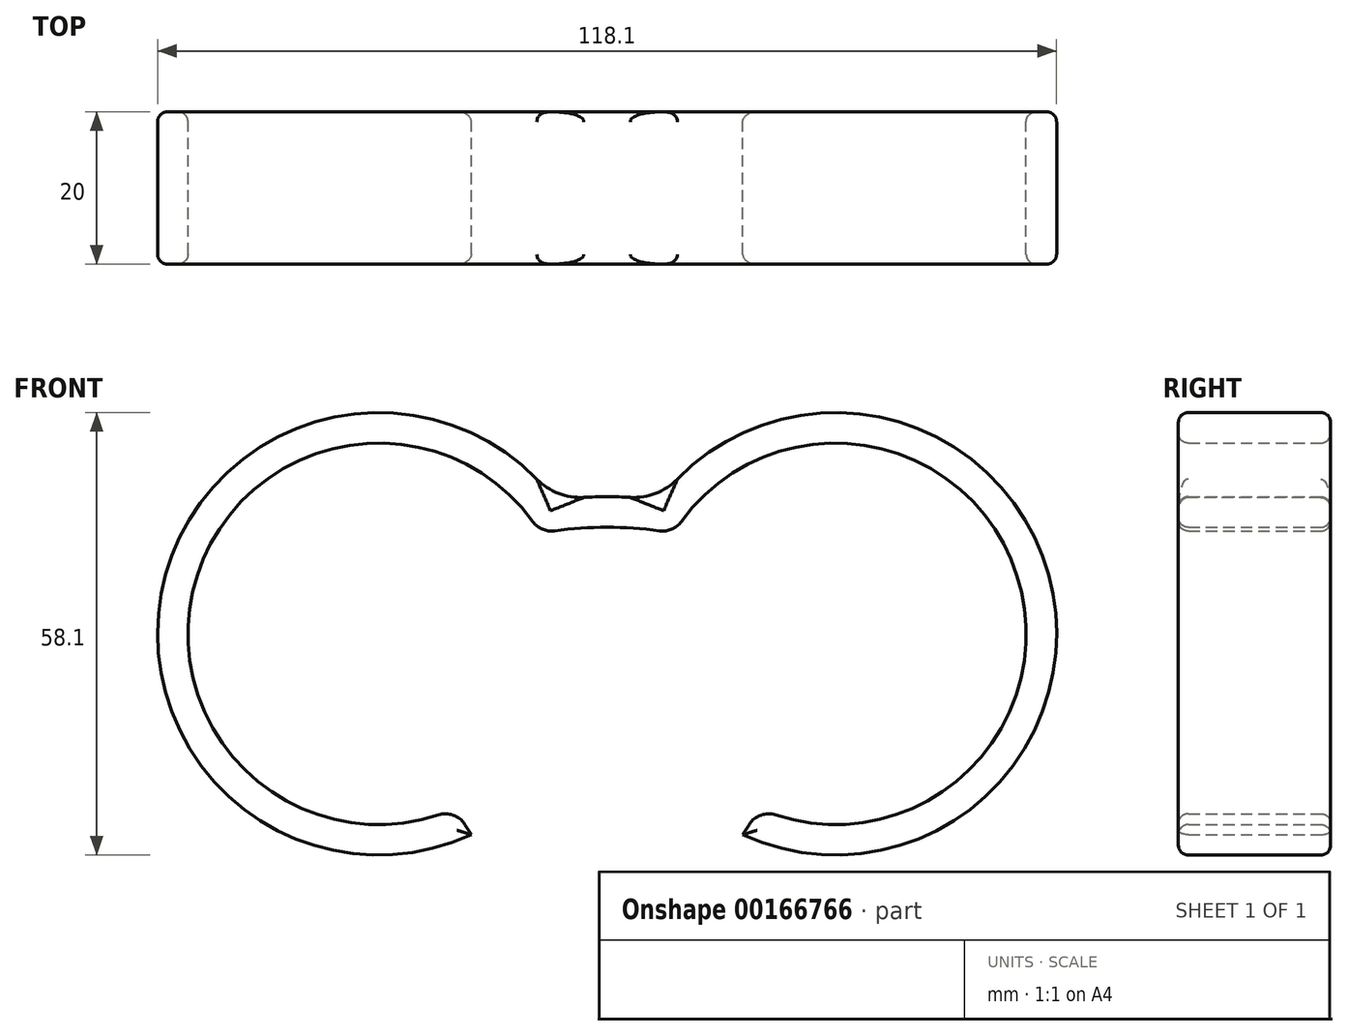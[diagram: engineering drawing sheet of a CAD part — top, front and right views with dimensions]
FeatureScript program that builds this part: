
annotation { "Feature Type Name" : "Feature", "Feature Type Description" : "" }
export const myFeature = defineFeature(function(context is Context, id is Id, definition is map)
    precondition{}
    {
        {
            var Q0;
            Q0=qCreatedBy(makeId("Front.planeOp"),FACE);
            var sketch = newSketch(context, id + "F0", { "sketchPlane" : qUnion([Q0])});
            skArc(sketch, "E0", {"start": v(0, 0) * mm, "mid": v(3.46, -0.12) * mm, "end": v(6.9, -0.48) * mm});
            skLineSegment(sketch, "E1", {"start": v(-31.28, -14) * mm, "end": v(36.53, -14) * mm, "construction": true});
            skPoint(sketch, "E2", {"position": v(30, -14) * mm});
            skLineSegment(sketch, "E3", {"start": v(20, -52.37) * mm, "end": v(20, 23.3) * mm, "construction": true});
            skArc(sketch, "E4", {"start": v(9.74, 0.73) * mm, "mid": v(53.84, -6.31) * mm, "end": v(22.15, -37.8) * mm});
            skArc(sketch, "E5.0", {"start": v(6.86, 3.56) * mm, "mid": v(58.19, -6.97) * mm, "end": v(17.82, -40.37) * mm});
            skArc(sketch, "E5.1", {"start": v(0, 4) * mm, "mid": v(3.44, 3.9) * mm, "end": v(6.86, 3.56) * mm});
            skLineSegment(sketch, "E6", {"start": v(18.69, -39.02) * mm, "end": v(17.82, -40.37) * mm});
            skPoint(sketch, "E7.visualSharp", {"position": v(8.73, -0.77) * mm});
            skArc(sketch, "E7.filletArc", {"start": v(6.9, -0.48) * mm, "mid": v(8.48, -0.27) * mm, "end": v(9.74, 0.73) * mm});
            skPoint(sketch, "E8.visualSharp", {"position": v(20, -36.97) * mm});
            skArc(sketch, "E8.filletArc", {"start": v(22.15, -37.8) * mm, "mid": v(20.2, -37.81) * mm, "end": v(18.69, -39.02) * mm});
            skLineSegment(sketch, "E9.MirrorCS", {"start": v(-18.69, -39.02) * mm, "end": v(-17.82, -40.37) * mm});
            skArc(sketch, "E10.MirrorCS", {"start": v(-22.15, -37.8) * mm, "mid": v(-20.2, -37.81) * mm, "end": v(-18.69, -39.02) * mm});
            skArc(sketch, "E11.MirrorCS", {"start": v(-6.9, -0.48) * mm, "mid": v(-8.48, -0.27) * mm, "end": v(-9.74, 0.73) * mm});
            skArc(sketch, "E12.MirrorCS", {"start": v(-6.86, 3.56) * mm, "mid": v(-58.19, -6.97) * mm, "end": v(-17.82, -40.37) * mm});
            skPoint(sketch, "E13.MirrorP", {"position": v(-20, -36.97) * mm});
            skArc(sketch, "E14.MirrorCS", {"start": v(0, 0) * mm, "mid": v(-3.46, -0.12) * mm, "end": v(-6.9, -0.48) * mm});
            skPoint(sketch, "E15.MirrorP", {"position": v(-8.73, -0.77) * mm});
            skArc(sketch, "E16.MirrorCS", {"start": v(-9.74, 0.73) * mm, "mid": v(-53.84, -6.31) * mm, "end": v(-22.15, -37.8) * mm});
            skArc(sketch, "E17.MirrorCS", {"start": v(0, 4) * mm, "mid": v(-3.44, 3.9) * mm, "end": v(-6.86, 3.56) * mm});
            skSolve(sketch);
        }
        {
            var Q0;
            Q0 = qSketchRegion(id + "F0", true);
            extrude(context, id + "F1", {"entities" : qUnion([Q0]), "depth" : 20 * mm});
        }
        {
            var Q0;
            Q0=makeQuery(id+"F1.opExtrude","CAP_FACE",FACE,{"disambiguationData":[OSD([sQuery(id+"F0.wireOp",EDGE,"E0"),sQuery(id+"F0.wireOp",EDGE,"E4"),sQuery(id+"F0.wireOp",EDGE,"E5.0"),sQuery(id+"F0.wireOp",EDGE,"E5.1"),sQuery(id+"F0.wireOp",EDGE,"E6"),sQuery(id+"F0.wireOp",EDGE,"E7.filletArc"),sQuery(id+"F0.wireOp",EDGE,"E8.filletArc"),sQuery(id+"F0.wireOp",EDGE,"E9.MirrorCS"),sQuery(id+"F0.wireOp",EDGE,"E10.MirrorCS"),sQuery(id+"F0.wireOp",EDGE,"E11.MirrorCS"),sQuery(id+"F0.wireOp",EDGE,"E12.MirrorCS"),sQuery(id+"F0.wireOp",EDGE,"E14.MirrorCS"),sQuery(id+"F0.wireOp",EDGE,"E16.MirrorCS"),sQuery(id+"F0.wireOp",EDGE,"E17.MirrorCS")])],"isStart":false});
            var Q1;
            Q1=makeQuery(id+"F1.opExtrude","CAP_FACE",FACE,{"disambiguationData":[OSD([sQuery(id+"F0.wireOp",EDGE,"E0"),sQuery(id+"F0.wireOp",EDGE,"E4"),sQuery(id+"F0.wireOp",EDGE,"E5.0"),sQuery(id+"F0.wireOp",EDGE,"E5.1"),sQuery(id+"F0.wireOp",EDGE,"E6"),sQuery(id+"F0.wireOp",EDGE,"E7.filletArc"),sQuery(id+"F0.wireOp",EDGE,"E8.filletArc"),sQuery(id+"F0.wireOp",EDGE,"E9.MirrorCS"),sQuery(id+"F0.wireOp",EDGE,"E10.MirrorCS"),sQuery(id+"F0.wireOp",EDGE,"E11.MirrorCS"),sQuery(id+"F0.wireOp",EDGE,"E12.MirrorCS"),sQuery(id+"F0.wireOp",EDGE,"E14.MirrorCS"),sQuery(id+"F0.wireOp",EDGE,"E16.MirrorCS"),sQuery(id+"F0.wireOp",EDGE,"E17.MirrorCS")])],"isStart":true});
            fillet(context, id + "F2", {"entities" : qUnion([Q0, Q1]), "radius" : 1.3 * mm, "tangentPropagation" : true, "allowEdgeOverflow" : false});
        }
        {
            var Q0;
            Q0=makeQuery(id+"F1.opExtrude","SWEPT_EDGE",EDGE,{"disambiguationData":[OSD([sQuery(id+"F0.wireOp",EDGE,"E5.0"),sQuery(id+"F0.wireOp",EDGE,"E5.1")])]});
            var Q1;
            Q1=makeQuery(id+"F1.opExtrude","SWEPT_EDGE",EDGE,{"disambiguationData":[OSD([sQuery(id+"F0.wireOp",EDGE,"E12.MirrorCS"),sQuery(id+"F0.wireOp",EDGE,"E17.MirrorCS")])]});
            fillet(context, id + "F3", {"entities" : qUnion([Q0, Q1]), "radius" : 8 * mm, "tangentPropagation" : true, "allowEdgeOverflow" : false});
        }
    });
